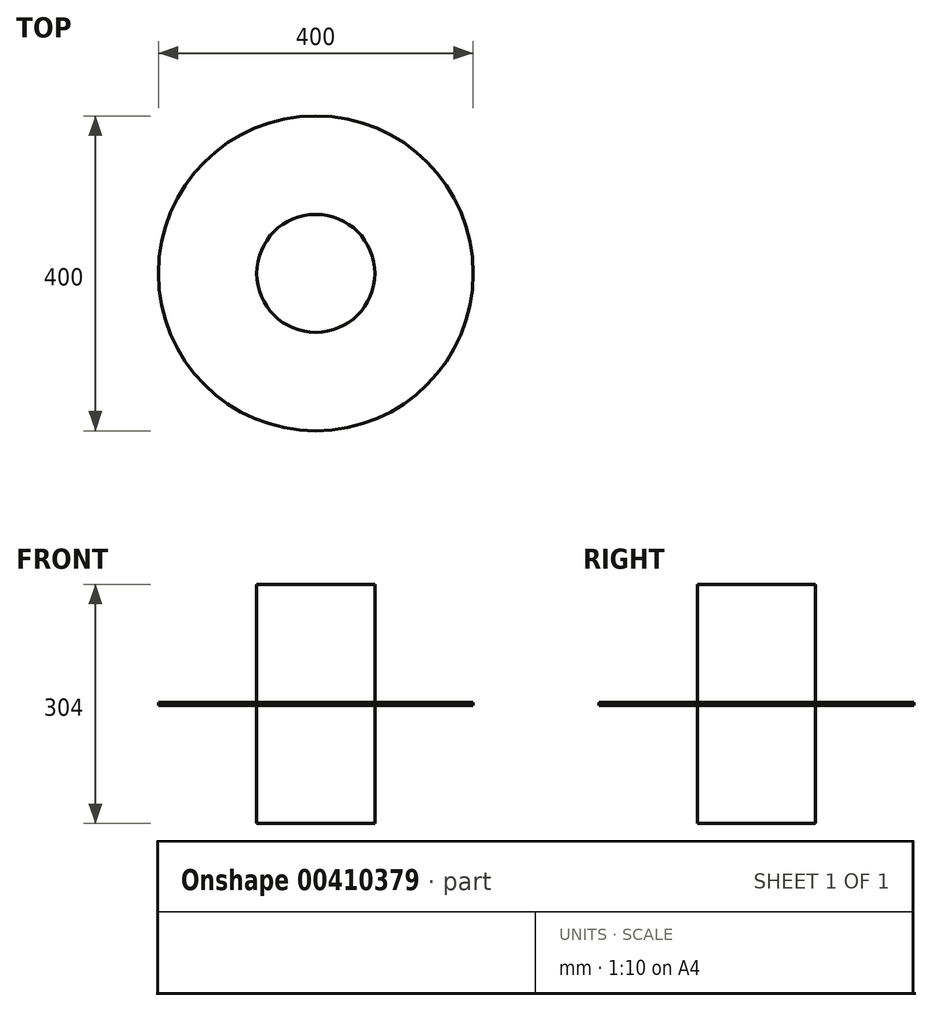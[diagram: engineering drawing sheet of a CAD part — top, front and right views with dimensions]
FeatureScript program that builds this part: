
annotation { "Feature Type Name" : "Feature", "Feature Type Description" : "" }
export const myFeature = defineFeature(function(context is Context, id is Id, definition is map)
    precondition{}
    {
        {
            var Q0;
            Q0=qCreatedBy(makeId("Top.planeOp"),FACE);
            var sketch = newSketch(context, id + "F0", { "sketchPlane" : qUnion([Q0])});
            skCircle(sketch, "E0", {"center": v(0, 0) * mm, "radius": 200 * mm});
            skSolve(sketch);
        }
        {
            var Q0;
            Q0=makeQuery(id+"F0.imprint","IMPRINT",FACE,{"disambiguationData":[TD([[makeQuery(id+"F0.imprint","IMPRINT",EDGE,{"derivedFrom":sQuery(id+"F0.wireOp",EDGE,"E0")}),1.0]])]});
            extrude(context, id + "F1", {"entities" : qUnion([Q0]), "depth" : 2 * mm});
        }
        {
            var Q0;
            Q0=makeQuery(id+"F1.opExtrude","CAP_FACE",FACE,{"disambiguationData":[OSD([sQuery(id+"F0.wireOp",EDGE,"E0")])],"isStart":false});
            var sketch = newSketch(context, id + "F2", { "sketchPlane" : qUnion([Q0])});
            skCircle(sketch, "E1", {"center": v(0, 0) * mm, "radius": 75 * mm});
            skSolve(sketch);
        }
        {
            var Q0;
            Q0 = qSketchRegion(id + "F2", true);
            extrude(context, id + "F3", {"entities" : qUnion([Q0]), "operationType" : NewBodyOperationType.ADD, "depth" : 150 * mm});
        }
        {
            var Q0;
            Q0=makeQuery(id+"F1.opExtrude","SWEPT_BODY",BODY,{"disambiguationData":[OSD([sQuery(id+"F0.wireOp",EDGE,"E0")])]});
            var Q1;
            Q1=makeQuery(id+"F0.imprint","IMPRINT",FACE,{"disambiguationData":[TD([[makeQuery(id+"F0.imprint","IMPRINT",EDGE,{"derivedFrom":sQuery(id+"F0.wireOp",EDGE,"E0")}),1.0]])]});
            mirror(context, id + "F4", {"operationType" : NewBodyOperationType.ADD, "entities" : qUnion([Q0]), "mirrorPlane" : qUnion([Q1])});
        }
    });
